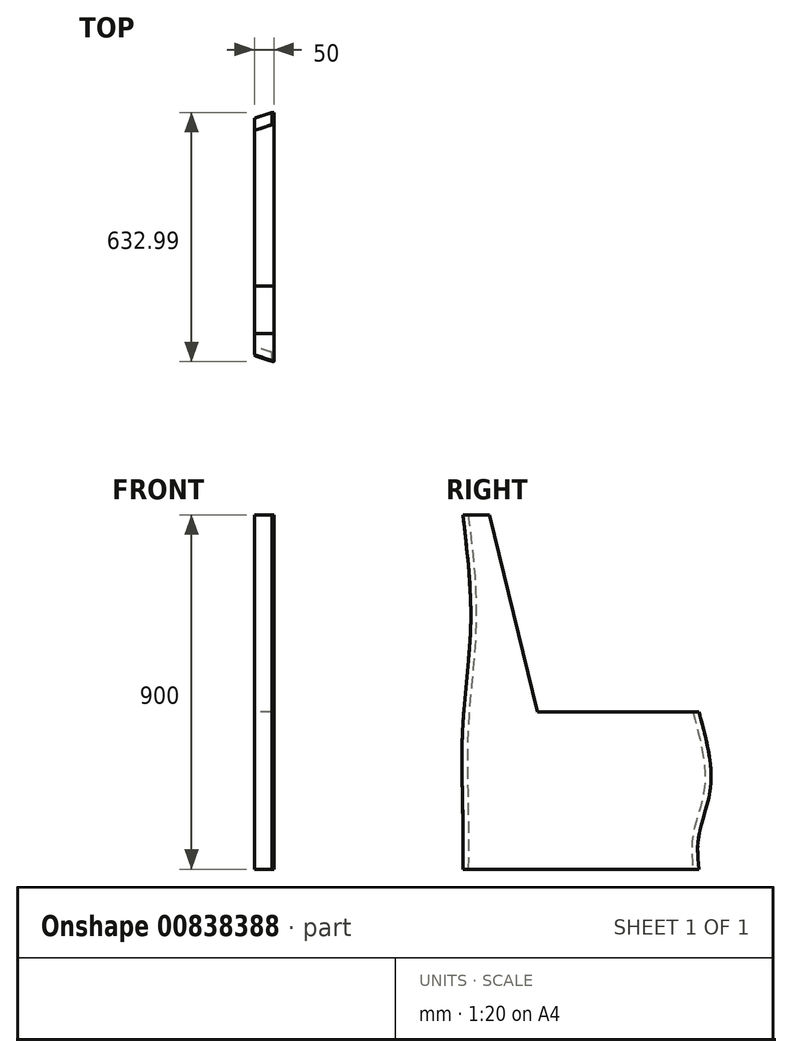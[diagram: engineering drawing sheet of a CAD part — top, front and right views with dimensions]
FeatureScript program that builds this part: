
annotation { "Feature Type Name" : "Feature", "Feature Type Description" : "" }
export const myFeature = defineFeature(function(context is Context, id is Id, definition is map)
    precondition{}
    {
        {
            var Q0;
            Q0=qCreatedBy(makeId("Right.planeOp"),FACE);
            var sketch = newSketch(context, id + "F0", { "sketchPlane" : qUnion([Q0])});
            skLineSegment(sketch, "E0.bottom", {"start": v(0, 0) * mm, "end": v(600, 0) * mm});
            skLineSegment(sketch, "E0.top", {"start": v(0, 900) * mm, "end": v(68.28, 900) * mm});
            skLineSegment(sketch, "E1", {"start": v(68.28, 900) * mm, "end": v(189.2, 400) * mm});
            skLineSegment(sketch, "E2", {"start": v(189.2, 400) * mm, "end": v(600, 400) * mm});
            skFitSpline(sketch, "E3", {"points": [v(0, 900) * mm, v(20.41, 631.11) * mm, v(0, 364.09) * mm, v(0, 147.44) * mm, v(0, 0) * mm], "startDerivative": vector(119.8, -973.56) * mm, "endDerivative": vector(-6.86, -692.77) * mm});
            skFitSpline(sketch, "E4", {"points": [v(600, 400) * mm, v(630.04, 215.46) * mm, v(600, 86.98) * mm, v(600, 0) * mm], "startDerivative": vector(131.1, -483.42) * mm, "endDerivative": vector(30.62, -310.67) * mm});
            skSolve(sketch);
        }
        {
            var Q0;
            Q0=qSketchRegion(id+"F0",true);
            extrude(context, id + "F1", {"entities" : qUnion([Q0]), "depth" : 50 * mm, "offsetDistance" : 25 * mm});
        }
        {
            var Q0;
            Q0=makeQuery(id+"F1.opExtrude","CAP_EDGE",EDGE,{"disambiguationData":[OSD([sQuery(id+"F0.wireOp",EDGE,"E3")])],"isStart":true});
            var Q1;
            Q1=makeQuery(id+"F1.opExtrude","CAP_EDGE",EDGE,{"disambiguationData":[OSD([sQuery(id+"F0.wireOp",EDGE,"E4")])],"isStart":true});
            chamfer(context, id + "F2", {"entities" : qUnion([Q0, Q1]), "chamferType" : ChamferType.TWO_OFFSETS, "width1" : 45 * mm, "oppositeDirection" : false, "width2" : 15 * mm, "tangentPropagation" : true});
        }
    });
